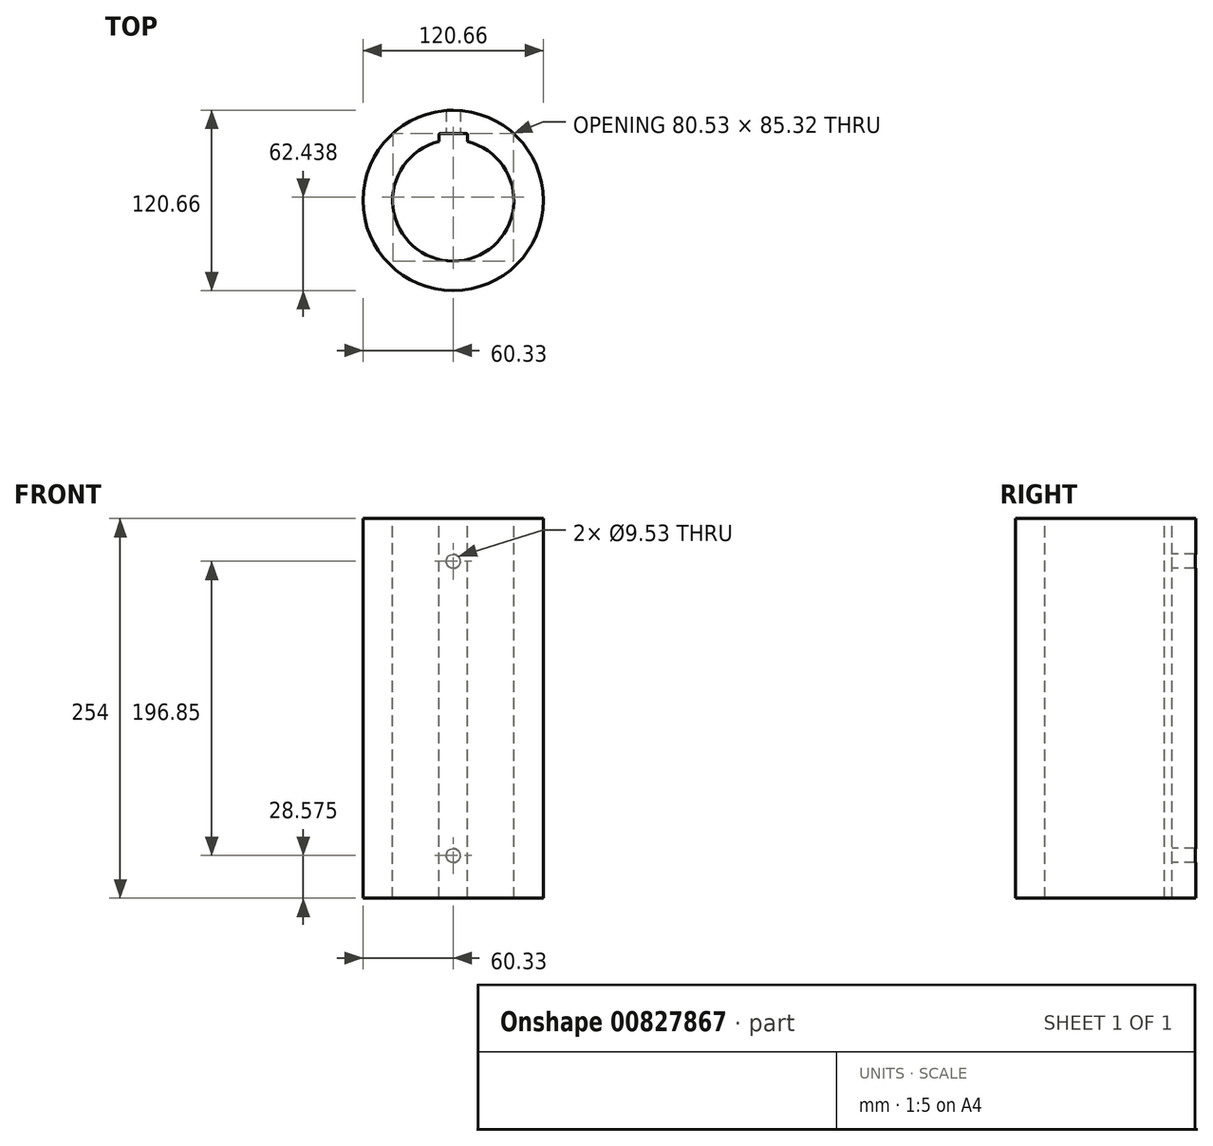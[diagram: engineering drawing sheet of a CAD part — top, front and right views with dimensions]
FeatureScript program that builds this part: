
annotation { "Feature Type Name" : "Feature", "Feature Type Description" : "" }
export const myFeature = defineFeature(function(context is Context, id is Id, definition is map)
    precondition{}
    {
        {
            var Q0;
            Q0=qCreatedBy(makeId("Top.planeOp"),FACE);
            var sketch = newSketch(context, id + "F0", { "sketchPlane" : qUnion([Q0])});
            skArc(sketch, "E0", {"start": v(-9.52, 39.42) * mm, "mid": v(0, -40.55) * mm, "end": v(9.52, 39.42) * mm});
            skLineSegment(sketch, "E1.top", {"start": v(-9.52, 44.77) * mm, "end": v(9.52, 44.77) * mm});
            skLineSegment(sketch, "E1.left", {"start": v(-9.53, 39.42) * mm, "end": v(-9.53, 44.77) * mm});
            skLineSegment(sketch, "E1.right", {"start": v(9.52, 39.42) * mm, "end": v(9.52, 44.77) * mm});
            skLineSegment(sketch, "E2", {"start": v(0, -67.6) * mm, "end": v(0, 44.77) * mm, "construction": true});
            skLineSegment(sketch, "E3", {"start": v(0, 0) * mm, "end": v(-85.03, 0) * mm, "construction": true});
            skCircle(sketch, "E4", {"center": v(0, 0) * mm, "radius": 60.33 * mm});
            skSolve(sketch);
        }
        {
            var Q0;
            Q0 = qSketchRegion(id + "F0", true);
            extrude(context, id + "F1", {"entities" : qUnion([Q0]), "oppositeDirection" : true, "depth" : 254 * mm, "offsetDistance" : 25.4 * mm});
        }
        {
            var Q0;
            Q0=qCreatedBy(makeId("Front.planeOp"),FACE);
            var sketch = newSketch(context, id + "F2", { "sketchPlane" : qUnion([Q0])});
            skLineSegment(sketch, "E5", {"start": v(0, 6.96) * mm, "end": v(0, -271.8) * mm, "construction": true});
            skCircle(sketch, "E6", {"center": v(0, -28.58) * mm, "radius": 4.76 * mm});
            skCircle(sketch, "E7", {"center": v(0, -225.42) * mm, "radius": 4.76 * mm});
            skSolve(sketch);
        }
        {
            var Q0;
            Q0 = qSketchRegion(id + "F2", true);
            extrude(context, id + "F3", {"entities" : qUnion([Q0]), "operationType" : NewBodyOperationType.REMOVE, "endBound" : BoundingType.THROUGH_ALL, "oppositeDirection" : true, "depth" : 131.57 * mm, "offsetDistance" : 25.4 * mm});
        }
        {
            var Q0;
            Q0=makeQuery(id+"F1.opExtrude","SWEPT_EDGE",EDGE,{"disambiguationData":[OSD([sQuery(id+"F0.wireOp",EDGE,"E1.top"),sQuery(id+"F0.wireOp",EDGE,"E1.left")])]});
            var Q1;
            Q1=makeQuery(id+"F1.opExtrude","SWEPT_EDGE",EDGE,{"disambiguationData":[OSD([sQuery(id+"F0.wireOp",EDGE,"E1.top"),sQuery(id+"F0.wireOp",EDGE,"E1.right")])]});
            fillet(context, id + "F4", {"entities" : qUnion([Q0, Q1]), "radius" : 0.76 * mm, "tangentPropagation" : true, "defaultsChanged" : true, "vertexSettings" : [], "allowEdgeOverflow" : false});
        }
    });
